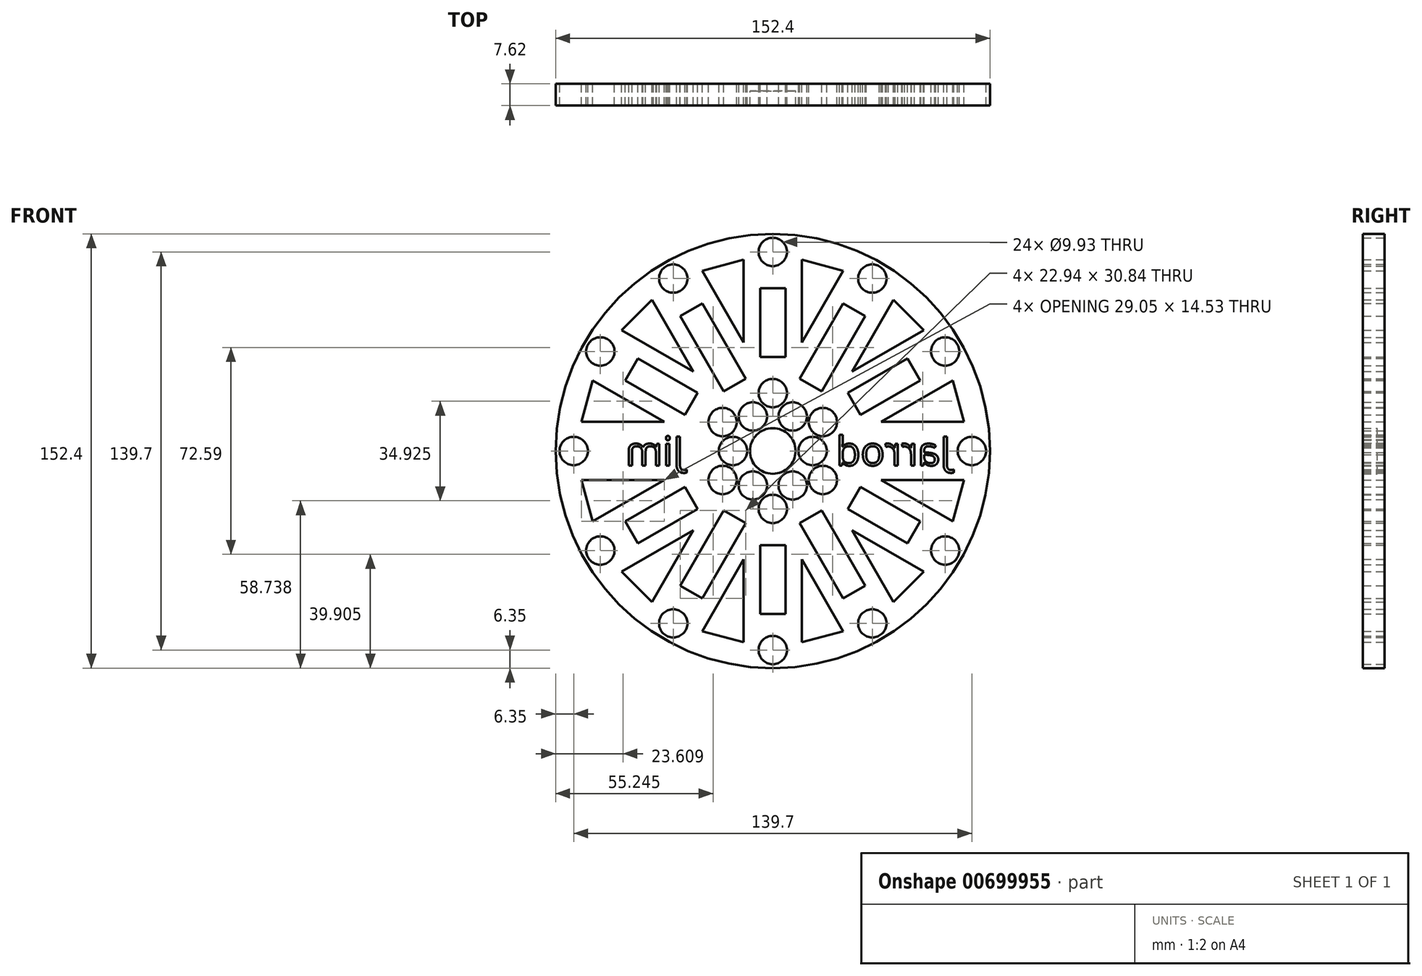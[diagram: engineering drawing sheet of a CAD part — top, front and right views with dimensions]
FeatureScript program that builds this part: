
annotation { "Feature Type Name" : "Feature", "Feature Type Description" : "" }
export const myFeature = defineFeature(function(context is Context, id is Id, definition is map)
    precondition{}
    {
        {
            var Q0;
            Q0=qCreatedBy(makeId("Front.planeOp"),FACE);
            var sketch = newSketch(context, id + "F0", { "sketchPlane" : qUnion([Q0])});
            skCircle(sketch, "E0", {"center": v(0, 0) * mm, "radius": 76.2 * mm});
            skCircle(sketch, "E1", {"center": v(0, 0) * mm, "radius": 8 * mm});
            skCircle(sketch, "E2", {"center": v(0, 69.85) * mm, "radius": 4.97 * mm});
            skCircle(sketch, "E3", {"center": v(0, 20.32) * mm, "radius": 4.97 * mm});
            skCircle(sketch, "E4.1.0", {"center": v(-60.5, 34.93) * mm, "radius": 4.97 * mm});
            skCircle(sketch, "E4.1.1", {"center": v(-17.6, 10.16) * mm, "radius": 4.97 * mm});
            skCircle(sketch, "E4.2.0", {"center": v(-60.5, -34.93) * mm, "radius": 4.97 * mm});
            skCircle(sketch, "E4.2.1", {"center": v(-17.6, -10.16) * mm, "radius": 4.97 * mm});
            skCircle(sketch, "E4.3.0", {"center": v(0, -69.85) * mm, "radius": 4.97 * mm});
            skCircle(sketch, "E4.3.1", {"center": v(0, -20.32) * mm, "radius": 4.97 * mm});
            skCircle(sketch, "E4.4.0", {"center": v(60.5, -34.93) * mm, "radius": 4.97 * mm});
            skCircle(sketch, "E4.4.1", {"center": v(17.6, -10.16) * mm, "radius": 4.97 * mm});
            skCircle(sketch, "E4.5.0", {"center": v(60.5, 34.93) * mm, "radius": 4.97 * mm});
            skCircle(sketch, "E4.5.1", {"center": v(17.6, 10.16) * mm, "radius": 4.97 * mm});
            skCircle(sketch, "E5", {"center": v(0, 0) * mm, "radius": 69.85 * mm, "construction": true});
            skCircle(sketch, "E6", {"center": v(-34.93, 60.5) * mm, "radius": 4.97 * mm});
            skLineSegment(sketch, "E7", {"start": v(-60.5, 34.92) * mm, "end": v(-34.92, 60.5) * mm, "construction": true});
            skLineSegment(sketch, "E8", {"start": v(-34.93, 60.5) * mm, "end": v(0, 69.85) * mm, "construction": true});
            skCircle(sketch, "E9.1.0", {"center": v(-69.85, 0) * mm, "radius": 4.97 * mm});
            skCircle(sketch, "E9.2.0", {"center": v(-34.93, -60.5) * mm, "radius": 4.97 * mm});
            skCircle(sketch, "E9.3.0", {"center": v(34.93, -60.5) * mm, "radius": 4.97 * mm});
            skCircle(sketch, "E9.4.0", {"center": v(69.85, 0) * mm, "radius": 4.97 * mm});
            skCircle(sketch, "E9.5.0", {"center": v(34.93, 60.5) * mm, "radius": 4.97 * mm});
            skCircle(sketch, "E10", {"center": v(-6.98, 12.1) * mm, "radius": 4.97 * mm});
            skLineSegment(sketch, "E11", {"start": v(-34.93, 60.5) * mm, "end": v(0, 0) * mm, "construction": true});
            skCircle(sketch, "E12.1.0", {"center": v(-13.97, 0) * mm, "radius": 4.97 * mm});
            skCircle(sketch, "E12.2.0", {"center": v(-6.98, -12.1) * mm, "radius": 4.97 * mm});
            skCircle(sketch, "E12.3.0", {"center": v(6.99, -12.1) * mm, "radius": 4.97 * mm});
            skCircle(sketch, "E12.4.0", {"center": v(13.97, 0) * mm, "radius": 4.97 * mm});
            skCircle(sketch, "E12.5.0", {"center": v(6.99, 12.1) * mm, "radius": 4.97 * mm});
            skCircle(sketch, "E13", {"center": v(0, 0) * mm, "radius": 2.5 * mm});
            skLineSegment(sketch, "E14", {"start": v(0, 69.85) * mm, "end": v(0, 20.32) * mm, "construction": true});
            skLineSegment(sketch, "E15.bottom", {"start": v(-4.45, 33.02) * mm, "end": v(4.44, 33.02) * mm});
            skLineSegment(sketch, "E15.top", {"start": v(-4.45, 57.15) * mm, "end": v(4.44, 57.15) * mm});
            skLineSegment(sketch, "E15.left", {"start": v(-4.45, 33.02) * mm, "end": v(-4.45, 57.15) * mm});
            skLineSegment(sketch, "E15.right", {"start": v(4.44, 33.02) * mm, "end": v(4.44, 57.15) * mm});
            skPoint(sketch, "E15.middle", {"position": v(0, 45.08) * mm});
            skLineSegment(sketch, "E16", {"start": v(6.99, 12.1) * mm, "end": v(34.92, 60.5) * mm, "construction": true});
            skPoint(sketch, "E17.middle", {"position": v(20.96, 36.3) * mm});
            skLineSegment(sketch, "E18.bottom", {"start": v(24.73, 51.72) * mm, "end": v(32.42, 47.27) * mm});
            skLineSegment(sketch, "E18.top", {"start": v(9.49, 25.32) * mm, "end": v(17.18, 20.87) * mm});
            skLineSegment(sketch, "E18.left", {"start": v(24.73, 51.72) * mm, "end": v(9.49, 25.32) * mm});
            skLineSegment(sketch, "E18.right", {"start": v(32.42, 47.27) * mm, "end": v(17.18, 20.87) * mm});
            skLineSegment(sketch, "E19.1.0", {"start": v(-30.82, 12.66) * mm, "end": v(-51.72, 24.73) * mm});
            skLineSegment(sketch, "E19.1.1", {"start": v(-26.37, 20.36) * mm, "end": v(-47.27, 32.42) * mm});
            skLineSegment(sketch, "E19.1.2", {"start": v(-30.82, 12.66) * mm, "end": v(-26.37, 20.36) * mm});
            skLineSegment(sketch, "E19.1.3", {"start": v(-51.72, 24.73) * mm, "end": v(-47.27, 32.42) * mm});
            skLineSegment(sketch, "E19.1.4", {"start": v(-32.42, 47.27) * mm, "end": v(-24.73, 51.72) * mm});
            skLineSegment(sketch, "E19.1.5", {"start": v(-32.42, 47.27) * mm, "end": v(-17.18, 20.87) * mm});
            skLineSegment(sketch, "E19.1.6", {"start": v(-24.73, 51.72) * mm, "end": v(-9.49, 25.32) * mm});
            skLineSegment(sketch, "E19.1.7", {"start": v(-17.18, 20.87) * mm, "end": v(-9.49, 25.32) * mm});
            skLineSegment(sketch, "E19.2.0", {"start": v(-26.37, -20.36) * mm, "end": v(-47.27, -32.42) * mm});
            skLineSegment(sketch, "E19.2.1", {"start": v(-30.82, -12.66) * mm, "end": v(-51.72, -24.73) * mm});
            skLineSegment(sketch, "E19.2.2", {"start": v(-26.37, -20.36) * mm, "end": v(-30.82, -12.66) * mm});
            skLineSegment(sketch, "E19.2.3", {"start": v(-47.27, -32.42) * mm, "end": v(-51.72, -24.73) * mm});
            skLineSegment(sketch, "E19.2.4", {"start": v(-57.15, -4.45) * mm, "end": v(-57.15, 4.44) * mm, "construction": true});
            skLineSegment(sketch, "E19.2.5", {"start": v(-57.15, -4.45) * mm, "end": v(-26.67, -4.45) * mm, "construction": true});
            skLineSegment(sketch, "E19.2.6", {"start": v(-57.15, 4.44) * mm, "end": v(-26.67, 4.44) * mm, "construction": true});
            skLineSegment(sketch, "E19.2.7", {"start": v(-26.67, -4.45) * mm, "end": v(-26.67, 4.44) * mm, "construction": true});
            skLineSegment(sketch, "E19.3.0", {"start": v(4.45, -33.02) * mm, "end": v(4.45, -57.15) * mm});
            skLineSegment(sketch, "E19.3.1", {"start": v(-4.44, -33.02) * mm, "end": v(-4.44, -57.15) * mm});
            skLineSegment(sketch, "E19.3.2", {"start": v(4.45, -33.02) * mm, "end": v(-4.44, -33.02) * mm});
            skLineSegment(sketch, "E19.3.3", {"start": v(4.45, -57.15) * mm, "end": v(-4.44, -57.15) * mm});
            skLineSegment(sketch, "E19.3.4", {"start": v(-24.73, -51.72) * mm, "end": v(-32.42, -47.27) * mm});
            skLineSegment(sketch, "E19.3.5", {"start": v(-24.73, -51.72) * mm, "end": v(-9.49, -25.32) * mm});
            skLineSegment(sketch, "E19.3.6", {"start": v(-32.42, -47.27) * mm, "end": v(-17.18, -20.87) * mm});
            skLineSegment(sketch, "E19.3.7", {"start": v(-9.49, -25.32) * mm, "end": v(-17.18, -20.87) * mm});
            skLineSegment(sketch, "E19.4.0", {"start": v(30.82, -12.66) * mm, "end": v(51.72, -24.73) * mm});
            skLineSegment(sketch, "E19.4.1", {"start": v(26.37, -20.36) * mm, "end": v(47.27, -32.42) * mm});
            skLineSegment(sketch, "E19.4.2", {"start": v(30.82, -12.66) * mm, "end": v(26.37, -20.36) * mm});
            skLineSegment(sketch, "E19.4.3", {"start": v(51.72, -24.73) * mm, "end": v(47.27, -32.42) * mm});
            skLineSegment(sketch, "E19.4.4", {"start": v(32.42, -47.27) * mm, "end": v(24.73, -51.72) * mm});
            skLineSegment(sketch, "E19.4.5", {"start": v(32.42, -47.27) * mm, "end": v(17.18, -20.87) * mm});
            skLineSegment(sketch, "E19.4.6", {"start": v(24.73, -51.72) * mm, "end": v(9.49, -25.32) * mm});
            skLineSegment(sketch, "E19.4.7", {"start": v(17.18, -20.87) * mm, "end": v(9.49, -25.32) * mm});
            skLineSegment(sketch, "E19.5.0", {"start": v(26.37, 20.36) * mm, "end": v(47.27, 32.42) * mm});
            skLineSegment(sketch, "E19.5.1", {"start": v(30.82, 12.66) * mm, "end": v(51.72, 24.73) * mm});
            skLineSegment(sketch, "E19.5.2", {"start": v(26.37, 20.36) * mm, "end": v(30.82, 12.66) * mm});
            skLineSegment(sketch, "E19.5.3", {"start": v(47.27, 32.42) * mm, "end": v(51.72, 24.73) * mm});
            skLineSegment(sketch, "E19.5.4", {"start": v(57.15, 4.45) * mm, "end": v(57.15, -4.44) * mm, "construction": true});
            skLineSegment(sketch, "E19.5.5", {"start": v(57.15, 4.45) * mm, "end": v(26.67, 4.45) * mm, "construction": true});
            skLineSegment(sketch, "E19.5.6", {"start": v(57.15, -4.44) * mm, "end": v(26.67, -4.44) * mm, "construction": true});
            skLineSegment(sketch, "E19.5.7", {"start": v(26.67, 4.45) * mm, "end": v(26.67, -4.44) * mm, "construction": true});
            skSolve(sketch);
        }
        {
            var Q0;
            Q0=makeQuery(id+"F0.imprint","IMPRINT",FACE,{"disambiguationData":[TD([[makeQuery(id+"F0.imprint","IMPRINT",EDGE,{"derivedFrom":sQuery(id+"F0.wireOp",EDGE,"E0")}),1.0]])]});
            extrude(context, id + "F1", {"entities" : qUnion([Q0]), "depth" : 7.62 * mm, "offsetDistance" : 25.4 * mm});
        }
        {
            var Q0;
            Q0=makeQuery(id+"F1.opExtrude","CAP_FACE",FACE,{"disambiguationData":[OSD([sQuery(id+"F0.wireOp",EDGE,"E0"),sQuery(id+"F0.wireOp",EDGE,"E1"),sQuery(id+"F0.wireOp",EDGE,"E2"),sQuery(id+"F0.wireOp",EDGE,"E3"),sQuery(id+"F0.wireOp",EDGE,"E4.1.0"),sQuery(id+"F0.wireOp",EDGE,"E4.1.1"),sQuery(id+"F0.wireOp",EDGE,"E4.2.0"),sQuery(id+"F0.wireOp",EDGE,"E4.2.1"),sQuery(id+"F0.wireOp",EDGE,"E4.3.0"),sQuery(id+"F0.wireOp",EDGE,"E4.3.1"),sQuery(id+"F0.wireOp",EDGE,"E4.4.0"),sQuery(id+"F0.wireOp",EDGE,"E4.4.1"),sQuery(id+"F0.wireOp",EDGE,"E4.5.0"),sQuery(id+"F0.wireOp",EDGE,"E4.5.1"),sQuery(id+"F0.wireOp",EDGE,"E6"),sQuery(id+"F0.wireOp",EDGE,"E9.1.0"),sQuery(id+"F0.wireOp",EDGE,"E9.2.0"),sQuery(id+"F0.wireOp",EDGE,"E9.3.0"),sQuery(id+"F0.wireOp",EDGE,"E9.4.0"),sQuery(id+"F0.wireOp",EDGE,"E9.5.0"),sQuery(id+"F0.wireOp",EDGE,"E10"),sQuery(id+"F0.wireOp",EDGE,"E12.1.0"),sQuery(id+"F0.wireOp",EDGE,"E12.2.0"),sQuery(id+"F0.wireOp",EDGE,"E12.3.0"),sQuery(id+"F0.wireOp",EDGE,"E12.4.0"),sQuery(id+"F0.wireOp",EDGE,"E12.5.0")])],"isStart":true});
            var sketch = newSketch(context, id + "F2", { "sketchPlane" : qUnion([Q0])});
            skCircle(sketch, "E20", {"center": v(0, 0) * mm, "radius": 8 * mm});
            skSolve(sketch);
        }
        {
            var Q0;
            Q0=makeQuery(id+"F2.imprint","IMPRINT",FACE,{"disambiguationData":[TD([[makeQuery(id+"F2.imprint","IMPRINT",EDGE,{"derivedFrom":sQuery(id+"F2.wireOp",EDGE,"E20")}),-1.0]])]});
            extrude(context, id + "F3", {"entities" : qUnion([Q0]), "operationType" : NewBodyOperationType.ADD, "oppositeDirection" : true, "depth" : 2.54 * mm, "offsetDistance" : 25.4 * mm});
        }
        {
            var Q0;
            Q0=makeQuery(id+"F3.boolean.opBoolean","MERGE",FACE,{"derivedFrom":[makeQuery(id+"F1.opExtrude","CAP_FACE",FACE,{"disambiguationData":[OSD([sQuery(id+"F0.wireOp",EDGE,"E0"),sQuery(id+"F0.wireOp",EDGE,"E1"),sQuery(id+"F0.wireOp",EDGE,"E2"),sQuery(id+"F0.wireOp",EDGE,"E3"),sQuery(id+"F0.wireOp",EDGE,"E4.1.0"),sQuery(id+"F0.wireOp",EDGE,"E4.1.1"),sQuery(id+"F0.wireOp",EDGE,"E4.2.0"),sQuery(id+"F0.wireOp",EDGE,"E4.2.1"),sQuery(id+"F0.wireOp",EDGE,"E4.3.0"),sQuery(id+"F0.wireOp",EDGE,"E4.3.1"),sQuery(id+"F0.wireOp",EDGE,"E4.4.0"),sQuery(id+"F0.wireOp",EDGE,"E4.4.1"),sQuery(id+"F0.wireOp",EDGE,"E4.5.0"),sQuery(id+"F0.wireOp",EDGE,"E4.5.1"),sQuery(id+"F0.wireOp",EDGE,"E6"),sQuery(id+"F0.wireOp",EDGE,"E9.1.0"),sQuery(id+"F0.wireOp",EDGE,"E9.2.0"),sQuery(id+"F0.wireOp",EDGE,"E9.3.0"),sQuery(id+"F0.wireOp",EDGE,"E9.4.0"),sQuery(id+"F0.wireOp",EDGE,"E9.5.0"),sQuery(id+"F0.wireOp",EDGE,"E10"),sQuery(id+"F0.wireOp",EDGE,"E12.1.0"),sQuery(id+"F0.wireOp",EDGE,"E12.2.0"),sQuery(id+"F0.wireOp",EDGE,"E12.3.0"),sQuery(id+"F0.wireOp",EDGE,"E12.4.0"),sQuery(id+"F0.wireOp",EDGE,"E12.5.0"),sQuery(id+"F0.wireOp",EDGE,"E15.bottom"),sQuery(id+"F0.wireOp",EDGE,"E15.top"),sQuery(id+"F0.wireOp",EDGE,"E15.left"),sQuery(id+"F0.wireOp",EDGE,"E15.right"),sQuery(id+"F0.wireOp",EDGE,"E18.bottom"),sQuery(id+"F0.wireOp",EDGE,"E18.top"),sQuery(id+"F0.wireOp",EDGE,"E18.left"),sQuery(id+"F0.wireOp",EDGE,"E18.right"),sQuery(id+"F0.wireOp",EDGE,"E19.1.0"),sQuery(id+"F0.wireOp",EDGE,"E19.1.1"),sQuery(id+"F0.wireOp",EDGE,"E19.1.2"),sQuery(id+"F0.wireOp",EDGE,"E19.1.3"),sQuery(id+"F0.wireOp",EDGE,"E19.1.4"),sQuery(id+"F0.wireOp",EDGE,"E19.1.5"),sQuery(id+"F0.wireOp",EDGE,"E19.1.6"),sQuery(id+"F0.wireOp",EDGE,"E19.1.7"),sQuery(id+"F0.wireOp",EDGE,"E19.2.0"),sQuery(id+"F0.wireOp",EDGE,"E19.2.1"),sQuery(id+"F0.wireOp",EDGE,"E19.2.2"),sQuery(id+"F0.wireOp",EDGE,"E19.2.3"),sQuery(id+"F0.wireOp",EDGE,"E19.3.0"),sQuery(id+"F0.wireOp",EDGE,"E19.3.1"),sQuery(id+"F0.wireOp",EDGE,"E19.3.2"),sQuery(id+"F0.wireOp",EDGE,"E19.3.3"),sQuery(id+"F0.wireOp",EDGE,"E19.3.4"),sQuery(id+"F0.wireOp",EDGE,"E19.3.5"),sQuery(id+"F0.wireOp",EDGE,"E19.3.6"),sQuery(id+"F0.wireOp",EDGE,"E19.3.7"),sQuery(id+"F0.wireOp",EDGE,"E19.4.0"),sQuery(id+"F0.wireOp",EDGE,"E19.4.1"),sQuery(id+"F0.wireOp",EDGE,"E19.4.2"),sQuery(id+"F0.wireOp",EDGE,"E19.4.3"),sQuery(id+"F0.wireOp",EDGE,"E19.4.4"),sQuery(id+"F0.wireOp",EDGE,"E19.4.5"),sQuery(id+"F0.wireOp",EDGE,"E19.4.6"),sQuery(id+"F0.wireOp",EDGE,"E19.4.7"),sQuery(id+"F0.wireOp",EDGE,"E19.5.0"),sQuery(id+"F0.wireOp",EDGE,"E19.5.1"),sQuery(id+"F0.wireOp",EDGE,"E19.5.2"),sQuery(id+"F0.wireOp",EDGE,"E19.5.3")])],"isStart":true}),makeQuery(id+"F3.opExtrude","CAP_FACE",FACE,{"disambiguationData":[OSD([sQuery(id+"F2.wireOp",EDGE,"E20")])],"isStart":true})]});
            var sketch = newSketch(context, id + "F4", { "sketchPlane" : qUnion([Q0])});
            skText(sketch, "E21", { "text": "Jarrod", "fontName": "OpenSans-Regular.ttf"});
            skText(sketch, "E22", { "text": "Jim", "fontName": "OpenSans-Regular.ttf"});
            skPoint(sketch, "E23", {"position": v(41.9, 0) * mm});
            skPoint(sketch, "E24", {"position": v(-41.91, 0) * mm});
            skLineSegment(sketch, "E25", {"start": v(-69.85, 0) * mm, "end": v(-13.97, 0) * mm, "construction": true});
            skLineSegment(sketch, "E26", {"start": v(13.97, 0) * mm, "end": v(69.85, 0) * mm, "construction": true});
            const initialGuessF4  = {"E21": [-0.06247, -0.00508, 1, 0, 0.01016], "E22": [0.03124, -0.00508, 1, 0, 0.01016]};
            skSetInitialGuess(sketch, initialGuessF4);
            skSolve(sketch);
        }
        {
            var Q0;
            Q0 = qSketchRegion(id + "F4", true);
            extrude(context, id + "F5", {"entities" : qUnion([Q0]), "operationType" : NewBodyOperationType.REMOVE, "endBound" : BoundingType.THROUGH_ALL, "oppositeDirection" : true, "depth" : 25.4 * mm, "offsetDistance" : 25.4 * mm});
        }
        {
            var Q0;
            {var subQ0=sQuery(id+"F0.wireOp",EDGE,"E19.5.3");var subQ1=sQuery(id+"F0.wireOp",EDGE,"E19.5.2");var subQ2=sQuery(id+"F0.wireOp",EDGE,"E19.5.1");var subQ3=sQuery(id+"F0.wireOp",EDGE,"E19.5.0");var subQ4=sQuery(id+"F0.wireOp",EDGE,"E19.4.7");var subQ5=sQuery(id+"F0.wireOp",EDGE,"E19.4.6");var subQ6=sQuery(id+"F0.wireOp",EDGE,"E19.4.5");var subQ7=sQuery(id+"F0.wireOp",EDGE,"E19.4.4");var subQ8=sQuery(id+"F0.wireOp",EDGE,"E19.4.3");var subQ9=sQuery(id+"F0.wireOp",EDGE,"E19.4.2");var subQ10=sQuery(id+"F0.wireOp",EDGE,"E19.4.1");var subQ11=sQuery(id+"F0.wireOp",EDGE,"E19.4.0");var subQ12=sQuery(id+"F0.wireOp",EDGE,"E19.3.7");var subQ13=sQuery(id+"F0.wireOp",EDGE,"E19.3.6");var subQ14=sQuery(id+"F0.wireOp",EDGE,"E19.3.5");var subQ15=sQuery(id+"F0.wireOp",EDGE,"E19.3.4");var subQ16=sQuery(id+"F0.wireOp",EDGE,"E19.3.3");var subQ17=sQuery(id+"F0.wireOp",EDGE,"E19.3.2");var subQ18=sQuery(id+"F0.wireOp",EDGE,"E19.3.1");var subQ19=sQuery(id+"F0.wireOp",EDGE,"E12.2.0");var subQ20=sQuery(id+"F0.wireOp",EDGE,"E10");var subQ21=sQuery(id+"F0.wireOp",EDGE,"E9.5.0");var subQ22=sQuery(id+"F0.wireOp",EDGE,"E9.4.0");var subQ23=sQuery(id+"F0.wireOp",EDGE,"E9.3.0");var subQ24=sQuery(id+"F0.wireOp",EDGE,"E9.2.0");var subQ25=sQuery(id+"F0.wireOp",EDGE,"E9.1.0");var subQ26=sQuery(id+"F0.wireOp",EDGE,"E6");var subQ27=sQuery(id+"F0.wireOp",EDGE,"E4.5.1");var subQ28=sQuery(id+"F0.wireOp",EDGE,"E4.5.0");var subQ29=sQuery(id+"F0.wireOp",EDGE,"E4.4.1");var subQ30=sQuery(id+"F0.wireOp",EDGE,"E4.1.0");var subQ31=sQuery(id+"F0.wireOp",EDGE,"E2");var subQ32=sQuery(id+"F0.wireOp",EDGE,"E3");var subQ33=sQuery(id+"F0.wireOp",EDGE,"E12.1.0");var subQ34=sQuery(id+"F0.wireOp",EDGE,"E0");var subQ35=sQuery(id+"F0.wireOp",EDGE,"E19.2.3");var subQ36=sQuery(id+"F0.wireOp",EDGE,"E4.3.1");var subQ37=sQuery(id+"F0.wireOp",EDGE,"E4.1.1");var subQ38=sQuery(id+"F0.wireOp",EDGE,"E4.2.0");var subQ39=sQuery(id+"F0.wireOp",EDGE,"E4.2.1");var subQ40=sQuery(id+"F0.wireOp",EDGE,"E4.3.0");var subQ41=sQuery(id+"F0.wireOp",EDGE,"E4.4.0");var subQ42=sQuery(id+"F0.wireOp",EDGE,"E12.3.0");var subQ43=sQuery(id+"F0.wireOp",EDGE,"E12.4.0");var subQ44=sQuery(id+"F0.wireOp",EDGE,"E12.5.0");var subQ45=sQuery(id+"F0.wireOp",EDGE,"E15.bottom");var subQ46=sQuery(id+"F0.wireOp",EDGE,"E15.top");var subQ47=sQuery(id+"F0.wireOp",EDGE,"E15.left");var subQ48=sQuery(id+"F0.wireOp",EDGE,"E15.right");var subQ49=sQuery(id+"F0.wireOp",EDGE,"E18.bottom");var subQ50=sQuery(id+"F0.wireOp",EDGE,"E18.top");var subQ51=sQuery(id+"F0.wireOp",EDGE,"E18.left");var subQ52=sQuery(id+"F0.wireOp",EDGE,"E18.right");var subQ53=sQuery(id+"F0.wireOp",EDGE,"E19.1.0");var subQ54=sQuery(id+"F0.wireOp",EDGE,"E19.1.1");var subQ55=sQuery(id+"F0.wireOp",EDGE,"E19.1.2");var subQ56=sQuery(id+"F0.wireOp",EDGE,"E19.1.3");var subQ57=sQuery(id+"F0.wireOp",EDGE,"E19.1.4");var subQ58=sQuery(id+"F0.wireOp",EDGE,"E19.1.5");var subQ59=sQuery(id+"F0.wireOp",EDGE,"E19.1.6");var subQ60=sQuery(id+"F0.wireOp",EDGE,"E19.1.7");var subQ61=sQuery(id+"F0.wireOp",EDGE,"E19.2.0");var subQ62=sQuery(id+"F0.wireOp",EDGE,"E19.2.1");var subQ63=sQuery(id+"F0.wireOp",EDGE,"E19.2.2");var subQ64=sQuery(id+"F0.wireOp",EDGE,"E19.3.0");Q0=makeQuery(id+"F5.boolean.opBoolean","SPLIT",FACE,{"disambiguationData":[TD([makeQuery(id+"F1.opExtrude","SWEPT_FACE",FACE,{"disambiguationData":[OSD([subQ34])]})])],"derivedFrom":makeQuery(id+"F3.boolean.opBoolean","MERGE",FACE,{"derivedFrom":[makeQuery(id+"F1.opExtrude","CAP_FACE",FACE,{"disambiguationData":[OSD([subQ34,sQuery(id+"F0.wireOp",EDGE,"E1"),subQ31,subQ32,subQ30,subQ37,subQ38,subQ39,subQ40,subQ36,subQ41,subQ29,subQ28,subQ27,subQ26,subQ25,subQ24,subQ23,subQ22,subQ21,subQ20,subQ33,subQ19,subQ42,subQ43,subQ44,subQ45,subQ46,subQ47,subQ48,subQ49,subQ50,subQ51,subQ52,subQ53,subQ54,subQ55,subQ56,subQ57,subQ58,subQ59,subQ60,subQ61,subQ62,subQ63,subQ35,subQ64,subQ18,subQ17,subQ16,subQ15,subQ14,subQ13,subQ12,subQ11,subQ10,subQ9,subQ8,subQ7,subQ6,subQ5,subQ4,subQ3,subQ2,subQ1,subQ0])],"isStart":true}),makeQuery(id+"F3.opExtrude","CAP_FACE",FACE,{"disambiguationData":[OSD([sQuery(id+"F2.wireOp",EDGE,"E20")])],"isStart":true})]})});}
            var sketch = newSketch(context, id + "F6", { "sketchPlane" : qUnion([Q0])});
            skLineSegment(sketch, "E27", {"start": v(0, 69.85) * mm, "end": v(34.93, 60.5) * mm, "construction": true});
            skLineSegment(sketch, "E28", {"start": v(34.93, 60.5) * mm, "end": v(9.49, 25.32) * mm, "construction": true});
            skLineSegment(sketch, "E29", {"start": v(9.49, 25.32) * mm, "end": v(0, 69.85) * mm, "construction": true});
            skLineSegment(sketch, "E30", {"start": v(10.2, 38.06) * mm, "end": v(24.73, 63.22) * mm});
            skLineSegment(sketch, "E31", {"start": v(10.2, 67.12) * mm, "end": v(24.73, 63.22) * mm});
            skLineSegment(sketch, "E32", {"start": v(10.2, 67.12) * mm, "end": v(10.2, 38.06) * mm});
            skLineSegment(sketch, "E33", {"start": v(10.2, 67.12) * mm, "end": v(0, 69.85) * mm, "construction": true});
            skLineSegment(sketch, "E34", {"start": v(24.73, 63.22) * mm, "end": v(34.93, 60.5) * mm, "construction": true});
            skLineSegment(sketch, "E35.1.0", {"start": v(-24.73, 63.22) * mm, "end": v(-10.2, 38.06) * mm});
            skLineSegment(sketch, "E35.1.1", {"start": v(-34.92, 60.5) * mm, "end": v(0, 69.85) * mm, "construction": true});
            skLineSegment(sketch, "E35.1.2", {"start": v(-10.2, 38.06) * mm, "end": v(-10.2, 67.12) * mm});
            skLineSegment(sketch, "E35.2.0", {"start": v(-53.03, 42.4) * mm, "end": v(-27.87, 27.87) * mm});
            skLineSegment(sketch, "E35.2.1", {"start": v(-60.5, 34.93) * mm, "end": v(-34.93, 60.5) * mm, "construction": true});
            skLineSegment(sketch, "E35.2.2", {"start": v(-27.87, 27.87) * mm, "end": v(-42.4, 53.03) * mm});
            skLineSegment(sketch, "E35.3.0", {"start": v(-67.12, 10.2) * mm, "end": v(-38.06, 10.2) * mm});
            skLineSegment(sketch, "E35.3.1", {"start": v(-69.85, 0) * mm, "end": v(-60.5, 34.93) * mm, "construction": true});
            skLineSegment(sketch, "E35.3.2", {"start": v(-38.06, 10.2) * mm, "end": v(-63.22, 24.73) * mm});
            skLineSegment(sketch, "E35.4.0", {"start": v(-63.22, -24.73) * mm, "end": v(-38.06, -10.2) * mm});
            skLineSegment(sketch, "E35.4.1", {"start": v(-60.5, -34.92) * mm, "end": v(-69.85, 0) * mm, "construction": true});
            skLineSegment(sketch, "E35.4.2", {"start": v(-38.06, -10.2) * mm, "end": v(-67.12, -10.2) * mm});
            skLineSegment(sketch, "E35.5.0", {"start": v(-42.4, -53.03) * mm, "end": v(-27.87, -27.87) * mm});
            skLineSegment(sketch, "E35.5.1", {"start": v(-34.92, -60.5) * mm, "end": v(-60.5, -34.93) * mm, "construction": true});
            skLineSegment(sketch, "E35.5.2", {"start": v(-27.87, -27.87) * mm, "end": v(-53.03, -42.4) * mm});
            skLineSegment(sketch, "E35.6.0", {"start": v(-10.2, -67.12) * mm, "end": v(-10.2, -38.06) * mm});
            skLineSegment(sketch, "E35.6.1", {"start": v(0, -69.85) * mm, "end": v(-34.93, -60.5) * mm, "construction": true});
            skLineSegment(sketch, "E35.6.2", {"start": v(-10.2, -38.06) * mm, "end": v(-24.73, -63.22) * mm});
            skLineSegment(sketch, "E35.7.0", {"start": v(24.73, -63.22) * mm, "end": v(10.2, -38.06) * mm});
            skLineSegment(sketch, "E35.7.1", {"start": v(34.92, -60.5) * mm, "end": v(0, -69.85) * mm, "construction": true});
            skLineSegment(sketch, "E35.7.2", {"start": v(10.2, -38.06) * mm, "end": v(10.2, -67.12) * mm});
            skLineSegment(sketch, "E35.8.0", {"start": v(53.03, -42.4) * mm, "end": v(27.87, -27.87) * mm});
            skLineSegment(sketch, "E35.8.1", {"start": v(60.5, -34.93) * mm, "end": v(34.92, -60.5) * mm, "construction": true});
            skLineSegment(sketch, "E35.8.2", {"start": v(27.87, -27.87) * mm, "end": v(42.4, -53.03) * mm});
            skLineSegment(sketch, "E35.9.0", {"start": v(67.12, -10.2) * mm, "end": v(38.06, -10.2) * mm});
            skLineSegment(sketch, "E35.9.1", {"start": v(69.85, 0) * mm, "end": v(60.5, -34.93) * mm, "construction": true});
            skLineSegment(sketch, "E35.9.2", {"start": v(38.06, -10.2) * mm, "end": v(63.22, -24.73) * mm});
            skLineSegment(sketch, "E35.10.0", {"start": v(63.22, 24.73) * mm, "end": v(38.06, 10.2) * mm});
            skLineSegment(sketch, "E35.10.1", {"start": v(60.5, 34.93) * mm, "end": v(69.85, 0) * mm, "construction": true});
            skLineSegment(sketch, "E35.10.2", {"start": v(38.06, 10.2) * mm, "end": v(67.12, 10.2) * mm});
            skLineSegment(sketch, "E35.11.0", {"start": v(42.4, 53.03) * mm, "end": v(27.87, 27.87) * mm});
            skLineSegment(sketch, "E35.11.2", {"start": v(27.87, 27.87) * mm, "end": v(53.03, 42.4) * mm});
            skPoint(sketch, "E35.center", {"position": v(0, 0) * mm});
            skLineSegment(sketch, "E36", {"start": v(42.4, 53.03) * mm, "end": v(53.03, 42.4) * mm});
            skLineSegment(sketch, "E37.2.0", {"start": v(-24.73, 63.22) * mm, "end": v(-10.2, 67.12) * mm});
            skLineSegment(sketch, "E37.3.0", {"start": v(-53.03, 42.4) * mm, "end": v(-42.4, 53.03) * mm});
            skLineSegment(sketch, "E37.4.0", {"start": v(-67.12, 10.2) * mm, "end": v(-63.22, 24.73) * mm});
            skLineSegment(sketch, "E37.5.0", {"start": v(-63.22, -24.73) * mm, "end": v(-67.12, -10.2) * mm});
            skLineSegment(sketch, "E37.6.0", {"start": v(-42.4, -53.03) * mm, "end": v(-53.03, -42.4) * mm});
            skLineSegment(sketch, "E37.7.0", {"start": v(-10.2, -67.12) * mm, "end": v(-24.73, -63.22) * mm});
            skLineSegment(sketch, "E37.8.0", {"start": v(24.73, -63.22) * mm, "end": v(10.2, -67.12) * mm});
            skLineSegment(sketch, "E37.9.0", {"start": v(53.03, -42.4) * mm, "end": v(42.4, -53.03) * mm});
            skLineSegment(sketch, "E37.10.0", {"start": v(67.12, -10.2) * mm, "end": v(63.22, -24.73) * mm});
            skLineSegment(sketch, "E38.2.11.0", {"start": v(63.22, 24.73) * mm, "end": v(67.12, 10.2) * mm});
            skSolve(sketch);
        }
        {
            var Q0;
            Q0=makeQuery(id+"F6.imprint","IMPRINT",FACE,{"disambiguationData":[TD([[makeQuery(id+"F6.imprint","IMPRINT",EDGE,{"derivedFrom":sQuery(id+"F6.wireOp",EDGE,"E35.2.0")}),1.0]])]});
            var Q1;
            Q1=makeQuery(id+"F6.imprint","IMPRINT",FACE,{"disambiguationData":[TD([[makeQuery(id+"F6.imprint","IMPRINT",EDGE,{"derivedFrom":sQuery(id+"F6.wireOp",EDGE,"E35.3.0")}),1.0]])]});
            var Q2;
            Q2=makeQuery(id+"F6.imprint","IMPRINT",FACE,{"disambiguationData":[TD([[makeQuery(id+"F6.imprint","IMPRINT",EDGE,{"derivedFrom":sQuery(id+"F6.wireOp",EDGE,"E35.4.0")}),1.0]])]});
            var Q3;
            Q3=makeQuery(id+"F6.imprint","IMPRINT",FACE,{"disambiguationData":[TD([[makeQuery(id+"F6.imprint","IMPRINT",EDGE,{"derivedFrom":sQuery(id+"F6.wireOp",EDGE,"E35.5.0")}),1.0]])]});
            var Q4;
            Q4=makeQuery(id+"F6.imprint","IMPRINT",FACE,{"disambiguationData":[TD([[makeQuery(id+"F6.imprint","IMPRINT",EDGE,{"derivedFrom":sQuery(id+"F6.wireOp",EDGE,"E35.6.0")}),1.0]])]});
            var Q5;
            Q5=makeQuery(id+"F6.imprint","IMPRINT",FACE,{"disambiguationData":[TD([[makeQuery(id+"F6.imprint","IMPRINT",EDGE,{"derivedFrom":sQuery(id+"F6.wireOp",EDGE,"E35.7.0")}),1.0]])]});
            var Q6;
            Q6=makeQuery(id+"F6.imprint","IMPRINT",FACE,{"disambiguationData":[TD([[makeQuery(id+"F6.imprint","IMPRINT",EDGE,{"derivedFrom":sQuery(id+"F6.wireOp",EDGE,"E35.8.0")}),1.0]])]});
            var Q7;
            Q7=makeQuery(id+"F6.imprint","IMPRINT",FACE,{"disambiguationData":[TD([[makeQuery(id+"F6.imprint","IMPRINT",EDGE,{"derivedFrom":sQuery(id+"F6.wireOp",EDGE,"E35.9.0")}),1.0]])]});
            var Q8;
            Q8=makeQuery(id+"F6.imprint","IMPRINT",FACE,{"disambiguationData":[TD([[makeQuery(id+"F6.imprint","IMPRINT",EDGE,{"derivedFrom":sQuery(id+"F6.wireOp",EDGE,"E35.10.0")}),1.0]])]});
            var Q9;
            Q9=makeQuery(id+"F6.imprint","IMPRINT",FACE,{"disambiguationData":[TD([[makeQuery(id+"F6.imprint","IMPRINT",EDGE,{"derivedFrom":sQuery(id+"F6.wireOp",EDGE,"E35.11.0")}),1.0]])]});
            var Q10;
            Q10=makeQuery(id+"F6.imprint","IMPRINT",FACE,{"disambiguationData":[TD([[makeQuery(id+"F6.imprint","IMPRINT",EDGE,{"derivedFrom":sQuery(id+"F6.wireOp",EDGE,"E30")}),1.0]])]});
            var Q11;
            Q11=makeQuery(id+"F6.imprint","IMPRINT",FACE,{"disambiguationData":[TD([[makeQuery(id+"F6.imprint","IMPRINT",EDGE,{"derivedFrom":sQuery(id+"F6.wireOp",EDGE,"E35.1.0")}),1.0]])]});
            extrude(context, id + "F7", {"entities" : qUnion([Q0, Q1, Q2, Q3, Q4, Q5, Q6, Q7, Q8, Q9, Q10, Q11]), "operationType" : NewBodyOperationType.REMOVE, "endBound" : BoundingType.THROUGH_ALL, "oppositeDirection" : true, "depth" : 25.4 * mm, "offsetDistance" : 25.4 * mm});
        }
    });
